# Revit family: Valvula de bola_Aguilera Extincion
name_source: partatom
category: Accesorios de tuberías
revit_build: Autodesk Revit 2017 (Build: 20160225_1515(x64)
units: mm (PartAtom-declared; Revit-internal decimal feet)

## family parameters
Compartido = No
Corte con vacíos al cargar = No
Cota de conector redondo = Radio de uso
Número OmniClass = 23.65.55.14.17
Se basa en plano de trabajo = No
Siempre vertical = Sí
Tipo de pieza = Válvula - Se divide en
Título OmniClass = Adjusting/Controlling Valves for Liquid Services

## types (3) — shared parameters
A mm = 70 mm  [stored 0.229659 ft]
Descripción = Válvula By-Pass con rácores y un final de carrera.
Fabricante = Grupo Aguilera
Fin de carrera 2 = Sí
H mm = 138 mm  [stored 0.452756 ft]
L mm = 99 mm  [stored 0.324803 ft]
Simbolo = Sí
Símbolo texto = Sí
URL = http://aguilera.es

## per-type parameters (varying)
| type | D1 | D2 | D3 | D4 | Modelo | R1 | R2 | R3 | R4 | Radio |
| Válvula By-Pass de 16 (1/2") | 30 mm  [stored 0.0984252 ft] | 45 mm | 68 mm | 15 mm  [stored 0.0492126 ft] | AN/VBRF16 | 15 mm  [stored 0.0492126 ft] | 23 mm | 34 mm | 8 mm  [stored 0.0262467 ft] | 8 mm  [stored 0.0262467 ft] |
| Válvula By-Pass de 20 (3/4") | 34 mm | 51 mm | 77 mm | 17 mm | AN/VBRF20 | 17 mm | 26 mm | 38 mm | 9 mm  [stored 0.0295276 ft] | 10 mm  [stored 0.0328084 ft] |
| Válvula By-Pass de 30 (1 1/4") | 44 mm  [stored 0.144357 ft] | 66 mm | 99 mm  [stored 0.324803 ft] | 22 mm  [stored 0.0721785 ft] | AN/VBRF30 | 22 mm  [stored 0.0721785 ft] | 33 mm | 50 mm  [stored 0.164042 ft] | 11 mm  [stored 0.0360892 ft] | 15 mm  [stored 0.0492126 ft] |

note: [stored X ft] marks values corroborated as IEEE doubles in the binary element streams (Revit-internal decimal feet)

## geometry (parser evidence)
native form markers: Sweep x3
no freeform markers — native parametric forms only
